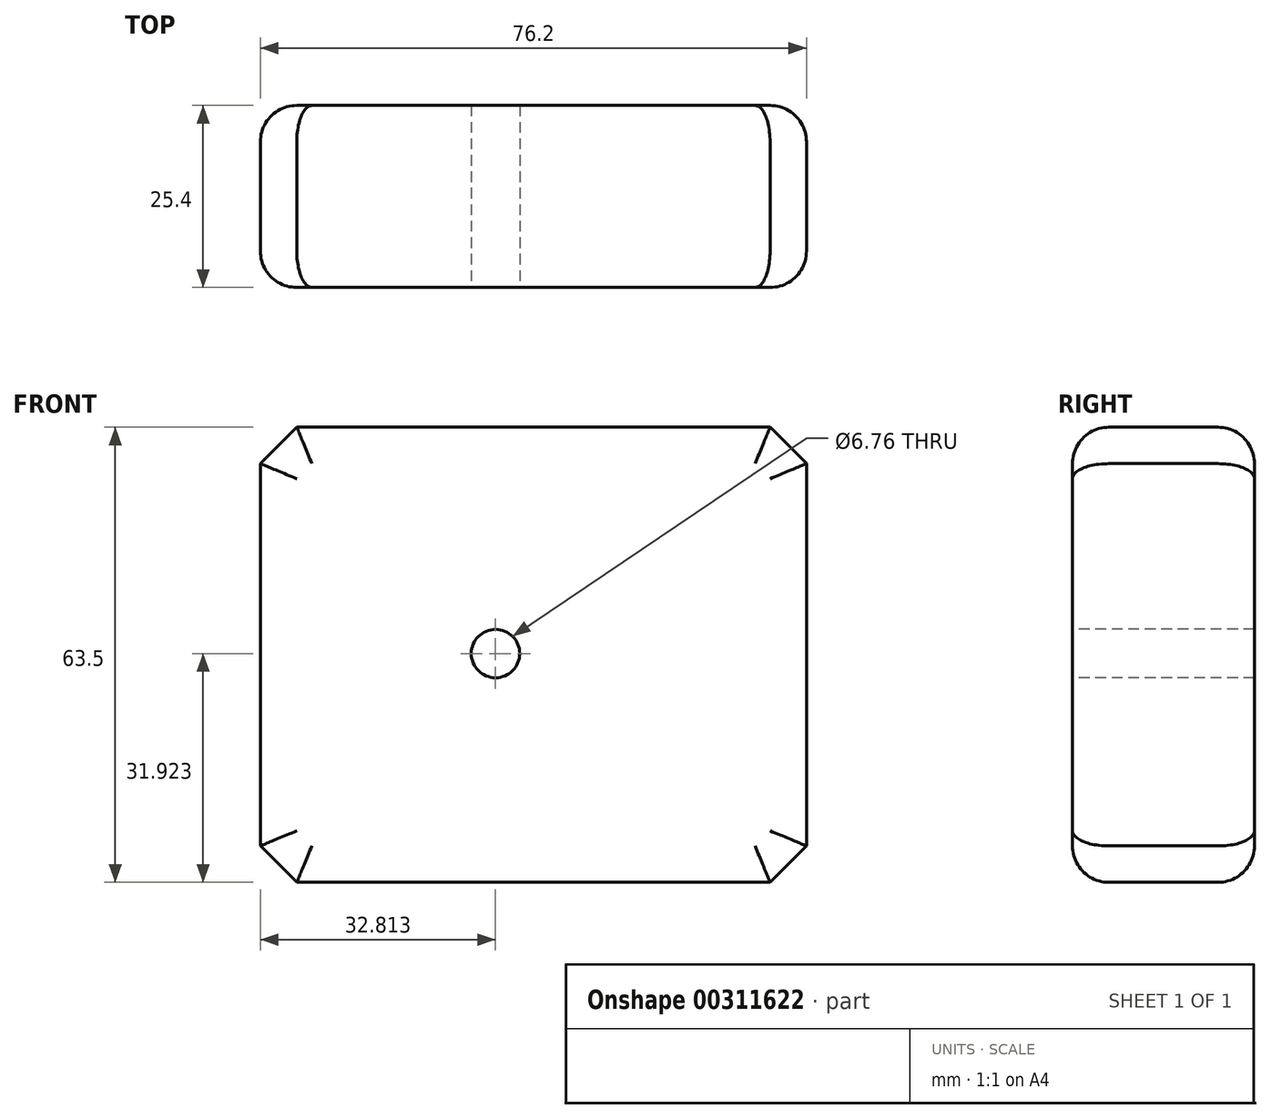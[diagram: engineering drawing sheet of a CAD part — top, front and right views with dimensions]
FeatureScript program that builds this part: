
annotation { "Feature Type Name" : "Feature", "Feature Type Description" : "" }
export const myFeature = defineFeature(function(context is Context, id is Id, definition is map)
    precondition{}
    {
        {
            var Q0;
            Q0=qCreatedBy(makeId("Front.planeOp"),FACE);
            var sketch = newSketch(context, id + "F0", { "sketchPlane" : qUnion([Q0])});
            skLineSegment(sketch, "E0", {"start": v(0, 0) * mm, "end": v(0, 63.5) * mm});
            skLineSegment(sketch, "E1", {"start": v(0, 63.5) * mm, "end": v(76.2, 63.5) * mm});
            skLineSegment(sketch, "E2", {"start": v(76.2, 63.5) * mm, "end": v(76.2, 0) * mm});
            skLineSegment(sketch, "E3", {"start": v(76.2, 0) * mm, "end": v(0, 0) * mm});
            skSolve(sketch);
        }
        {
            var Q0;
            Q0=makeQuery(id+"F0.imprint","IMPRINT",FACE,{"disambiguationData":[TD([[makeQuery(id+"F0.imprint","IMPRINT",EDGE,{"derivedFrom":sQuery(id+"F0.wireOp",EDGE,"E0")}),-1.0]])]});
            extrude(context, id + "F1", {"entities" : qUnion([Q0]), "depth" : 25.4 * mm});
        }
        {
            var Q0;
            Q0=makeQuery(id+"F1.opExtrude","SWEPT_EDGE",EDGE,{"disambiguationData":[OSD([sQuery(id+"F0.wireOp",EDGE,"E0"),sQuery(id+"F0.wireOp",EDGE,"E1")])]});
            var Q1;
            Q1=makeQuery(id+"F1.opExtrude","SWEPT_EDGE",EDGE,{"disambiguationData":[OSD([sQuery(id+"F0.wireOp",EDGE,"E1"),sQuery(id+"F0.wireOp",EDGE,"E2")])]});
            var Q2;
            Q2=makeQuery(id+"F1.opExtrude","SWEPT_EDGE",EDGE,{"disambiguationData":[OSD([sQuery(id+"F0.wireOp",EDGE,"E2"),sQuery(id+"F0.wireOp",EDGE,"E3")])]});
            var Q3;
            Q3=makeQuery(id+"F1.opExtrude","SWEPT_EDGE",EDGE,{"disambiguationData":[OSD([sQuery(id+"F0.wireOp",EDGE,"E0"),sQuery(id+"F0.wireOp",EDGE,"E3")])]});
            chamfer(context, id + "F2", {"entities" : qUnion([Q0, Q1, Q2, Q3]), "width" : 5.08 * mm, "tangentPropagation" : true});
        }
        {
            var Q0;
            Q0=makeQuery(id+"F1.opExtrude","CAP_EDGE",EDGE,{"disambiguationData":[OSD([sQuery(id+"F0.wireOp",EDGE,"E0")])],"isStart":false});
            var Q1;
            {var subQ0=sQuery(id+"F0.wireOp",EDGE,"E1");var subQ1=sQuery(id+"F0.wireOp",EDGE,"E0");Q1=makeQuery(id+"F2.opChamfer","BLEND_EDGE",EDGE,{"blendedFrom":[makeQuery(id+"F1.opExtrude","SWEPT_EDGE",EDGE,{"disambiguationData":[OSD([subQ1,subQ0])]}),makeQuery(id+"F1.opExtrude","CAP_FACE",FACE,{"disambiguationData":[OSD([subQ1,subQ0,sQuery(id+"F0.wireOp",EDGE,"E2"),sQuery(id+"F0.wireOp",EDGE,"E3")])],"isStart":false})],"blendedInto":[makeQuery(id+"F1.opExtrude","CAP_FACE",FACE,{"disambiguationData":[OSD([subQ1,subQ0,sQuery(id+"F0.wireOp",EDGE,"E2"),sQuery(id+"F0.wireOp",EDGE,"E3")])],"isStart":false})]});}
            var Q2;
            Q2=makeQuery(id+"F1.opExtrude","CAP_EDGE",EDGE,{"disambiguationData":[OSD([sQuery(id+"F0.wireOp",EDGE,"E1")])],"isStart":false});
            var Q3;
            {var subQ0=sQuery(id+"F0.wireOp",EDGE,"E2");var subQ1=sQuery(id+"F0.wireOp",EDGE,"E1");Q3=makeQuery(id+"F2.opChamfer","BLEND_EDGE",EDGE,{"blendedFrom":[makeQuery(id+"F1.opExtrude","SWEPT_EDGE",EDGE,{"disambiguationData":[OSD([subQ1,subQ0])]}),makeQuery(id+"F1.opExtrude","CAP_FACE",FACE,{"disambiguationData":[OSD([sQuery(id+"F0.wireOp",EDGE,"E0"),subQ1,subQ0,sQuery(id+"F0.wireOp",EDGE,"E3")])],"isStart":false})],"blendedInto":[makeQuery(id+"F1.opExtrude","CAP_FACE",FACE,{"disambiguationData":[OSD([sQuery(id+"F0.wireOp",EDGE,"E0"),subQ1,subQ0,sQuery(id+"F0.wireOp",EDGE,"E3")])],"isStart":false})]});}
            var Q4;
            Q4=makeQuery(id+"F1.opExtrude","CAP_EDGE",EDGE,{"disambiguationData":[OSD([sQuery(id+"F0.wireOp",EDGE,"E2")])],"isStart":false});
            var Q5;
            {var subQ0=sQuery(id+"F0.wireOp",EDGE,"E3");var subQ1=sQuery(id+"F0.wireOp",EDGE,"E2");Q5=makeQuery(id+"F2.opChamfer","BLEND_EDGE",EDGE,{"blendedFrom":[makeQuery(id+"F1.opExtrude","SWEPT_EDGE",EDGE,{"disambiguationData":[OSD([subQ1,subQ0])]}),makeQuery(id+"F1.opExtrude","CAP_FACE",FACE,{"disambiguationData":[OSD([sQuery(id+"F0.wireOp",EDGE,"E0"),sQuery(id+"F0.wireOp",EDGE,"E1"),subQ1,subQ0])],"isStart":false})],"blendedInto":[makeQuery(id+"F1.opExtrude","CAP_FACE",FACE,{"disambiguationData":[OSD([sQuery(id+"F0.wireOp",EDGE,"E0"),sQuery(id+"F0.wireOp",EDGE,"E1"),subQ1,subQ0])],"isStart":false})]});}
            var Q6;
            Q6=makeQuery(id+"F1.opExtrude","CAP_EDGE",EDGE,{"disambiguationData":[OSD([sQuery(id+"F0.wireOp",EDGE,"E3")])],"isStart":false});
            var Q7;
            {var subQ0=sQuery(id+"F0.wireOp",EDGE,"E3");var subQ1=sQuery(id+"F0.wireOp",EDGE,"E0");Q7=makeQuery(id+"F2.opChamfer","BLEND_EDGE",EDGE,{"blendedFrom":[makeQuery(id+"F1.opExtrude","SWEPT_EDGE",EDGE,{"disambiguationData":[OSD([subQ1,subQ0])]}),makeQuery(id+"F1.opExtrude","CAP_FACE",FACE,{"disambiguationData":[OSD([subQ1,sQuery(id+"F0.wireOp",EDGE,"E1"),sQuery(id+"F0.wireOp",EDGE,"E2"),subQ0])],"isStart":false})],"blendedInto":[makeQuery(id+"F1.opExtrude","CAP_FACE",FACE,{"disambiguationData":[OSD([subQ1,sQuery(id+"F0.wireOp",EDGE,"E1"),sQuery(id+"F0.wireOp",EDGE,"E2"),subQ0])],"isStart":false})]});}
            var Q8;
            Q8=makeQuery(id+"F1.opExtrude","CAP_EDGE",EDGE,{"disambiguationData":[OSD([sQuery(id+"F0.wireOp",EDGE,"E3")])],"isStart":true});
            var Q9;
            {var subQ0=sQuery(id+"F0.wireOp",EDGE,"E3");var subQ1=sQuery(id+"F0.wireOp",EDGE,"E0");Q9=makeQuery(id+"F2.opChamfer","BLEND_EDGE",EDGE,{"blendedFrom":[makeQuery(id+"F1.opExtrude","SWEPT_EDGE",EDGE,{"disambiguationData":[OSD([subQ1,subQ0])]}),makeQuery(id+"F1.opExtrude","CAP_FACE",FACE,{"disambiguationData":[OSD([subQ1,sQuery(id+"F0.wireOp",EDGE,"E1"),sQuery(id+"F0.wireOp",EDGE,"E2"),subQ0])],"isStart":true})],"blendedInto":[makeQuery(id+"F1.opExtrude","CAP_FACE",FACE,{"disambiguationData":[OSD([subQ1,sQuery(id+"F0.wireOp",EDGE,"E1"),sQuery(id+"F0.wireOp",EDGE,"E2"),subQ0])],"isStart":true})]});}
            var Q10;
            Q10=makeQuery(id+"F1.opExtrude","CAP_EDGE",EDGE,{"disambiguationData":[OSD([sQuery(id+"F0.wireOp",EDGE,"E0")])],"isStart":true});
            var Q11;
            {var subQ0=sQuery(id+"F0.wireOp",EDGE,"E1");var subQ1=sQuery(id+"F0.wireOp",EDGE,"E0");Q11=makeQuery(id+"F2.opChamfer","BLEND_EDGE",EDGE,{"blendedFrom":[makeQuery(id+"F1.opExtrude","SWEPT_EDGE",EDGE,{"disambiguationData":[OSD([subQ1,subQ0])]}),makeQuery(id+"F1.opExtrude","CAP_FACE",FACE,{"disambiguationData":[OSD([subQ1,subQ0,sQuery(id+"F0.wireOp",EDGE,"E2"),sQuery(id+"F0.wireOp",EDGE,"E3")])],"isStart":true})],"blendedInto":[makeQuery(id+"F1.opExtrude","CAP_FACE",FACE,{"disambiguationData":[OSD([subQ1,subQ0,sQuery(id+"F0.wireOp",EDGE,"E2"),sQuery(id+"F0.wireOp",EDGE,"E3")])],"isStart":true})]});}
            var Q12;
            Q12=makeQuery(id+"F1.opExtrude","CAP_EDGE",EDGE,{"disambiguationData":[OSD([sQuery(id+"F0.wireOp",EDGE,"E1")])],"isStart":true});
            var Q13;
            {var subQ0=sQuery(id+"F0.wireOp",EDGE,"E2");var subQ1=sQuery(id+"F0.wireOp",EDGE,"E1");Q13=makeQuery(id+"F2.opChamfer","BLEND_EDGE",EDGE,{"blendedFrom":[makeQuery(id+"F1.opExtrude","SWEPT_EDGE",EDGE,{"disambiguationData":[OSD([subQ1,subQ0])]}),makeQuery(id+"F1.opExtrude","CAP_FACE",FACE,{"disambiguationData":[OSD([sQuery(id+"F0.wireOp",EDGE,"E0"),subQ1,subQ0,sQuery(id+"F0.wireOp",EDGE,"E3")])],"isStart":true})],"blendedInto":[makeQuery(id+"F1.opExtrude","CAP_FACE",FACE,{"disambiguationData":[OSD([sQuery(id+"F0.wireOp",EDGE,"E0"),subQ1,subQ0,sQuery(id+"F0.wireOp",EDGE,"E3")])],"isStart":true})]});}
            var Q14;
            {var subQ0=sQuery(id+"F0.wireOp",EDGE,"E3");var subQ1=sQuery(id+"F0.wireOp",EDGE,"E2");Q14=makeQuery(id+"F2.opChamfer","BLEND_EDGE",EDGE,{"blendedFrom":[makeQuery(id+"F1.opExtrude","SWEPT_EDGE",EDGE,{"disambiguationData":[OSD([subQ1,subQ0])]}),makeQuery(id+"F1.opExtrude","CAP_FACE",FACE,{"disambiguationData":[OSD([sQuery(id+"F0.wireOp",EDGE,"E0"),sQuery(id+"F0.wireOp",EDGE,"E1"),subQ1,subQ0])],"isStart":true})],"blendedInto":[makeQuery(id+"F1.opExtrude","CAP_FACE",FACE,{"disambiguationData":[OSD([sQuery(id+"F0.wireOp",EDGE,"E0"),sQuery(id+"F0.wireOp",EDGE,"E1"),subQ1,subQ0])],"isStart":true})]});}
            var Q15;
            Q15=makeQuery(id+"F1.opExtrude","CAP_FACE",FACE,{"disambiguationData":[OSD([sQuery(id+"F0.wireOp",EDGE,"E0"),sQuery(id+"F0.wireOp",EDGE,"E1"),sQuery(id+"F0.wireOp",EDGE,"E2"),sQuery(id+"F0.wireOp",EDGE,"E3")])],"isStart":true});
            fillet(context, id + "F3", {"entities" : qUnion([Q0, Q1, Q2, Q3, Q4, Q5, Q6, Q7, Q8, Q9, Q10, Q11, Q12, Q13, Q14, Q15]), "radius" : 5.08 * mm, "tangentPropagation" : true, "allowEdgeOverflow" : false});
        }
        {
            var Q0;
            Q0=makeQuery(id+"F1.opExtrude","CAP_FACE",FACE,{"disambiguationData":[OSD([sQuery(id+"F0.wireOp",EDGE,"E0"),sQuery(id+"F0.wireOp",EDGE,"E1"),sQuery(id+"F0.wireOp",EDGE,"E2"),sQuery(id+"F0.wireOp",EDGE,"E3")])],"isStart":false});
            var sketch = newSketch(context, id + "F4", { "sketchPlane" : qUnion([Q0])});
            skPoint(sketch, "E4", {"position": v(32.81, 31.92) * mm});
            skSolve(sketch);
        }
        {
            var Q0;
            Q0=sQuery(id+"F4.wireOp",VERTEX,"E4");
            var Q1;
            Q1=makeQuery(id+"F1.opExtrude","SWEPT_BODY",BODY,{"disambiguationData":[OSD([sQuery(id+"F0.wireOp",EDGE,"E0"),sQuery(id+"F0.wireOp",EDGE,"E1"),sQuery(id+"F0.wireOp",EDGE,"E2"),sQuery(id+"F0.wireOp",EDGE,"E3")])]});
            hole(context, id + "F5", {"style" : HoleStyle.SIMPLE, "endStyle" : HoleEndStyle.THROUGH, "standardTappedOrClearance" : lookupTablePath({ "standard" : "ANSI", "fit" : "Normal (ASME)", "size" : "1/4", "type" : "Clearance" }), "standardBlindInLast" : lookupTablePath({ "fit" : "Free", "standard" : "ANSI", "size" : "1/4", "type" : "Clearance" }), "holeDiameter" : 6.76 * mm, "tappedDepth" : 12.7 * mm, "tapClearance" : 3, "locations" : qUnion([Q0]), "scope" : qUnion([Q1])});
        }
    });
